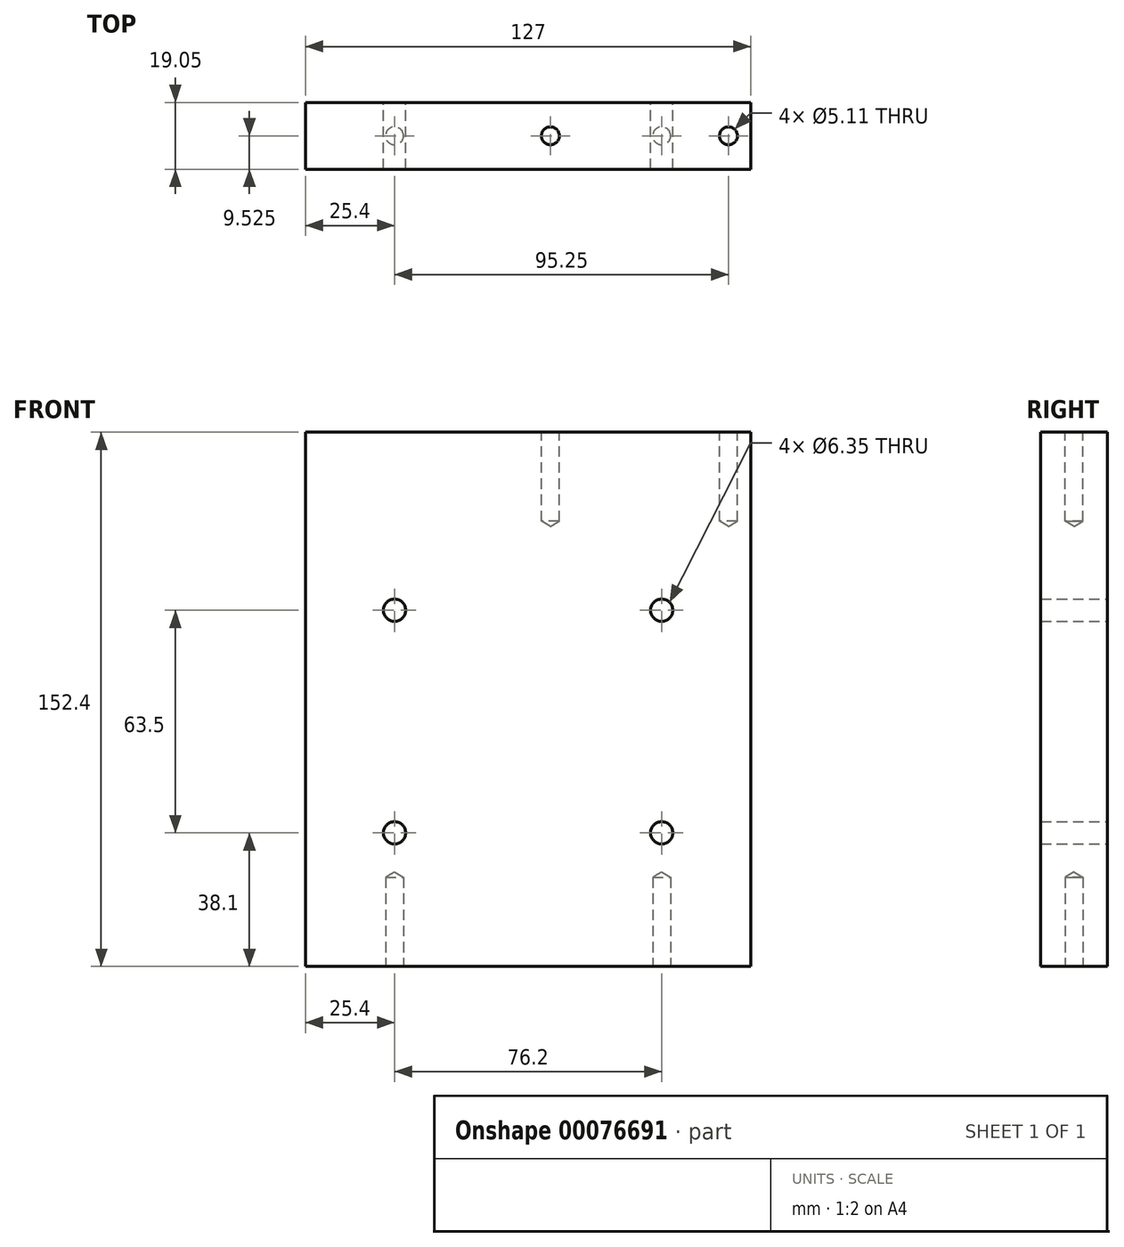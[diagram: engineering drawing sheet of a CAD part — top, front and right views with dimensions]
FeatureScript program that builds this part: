
annotation { "Feature Type Name" : "Feature", "Feature Type Description" : "" }
export const myFeature = defineFeature(function(context is Context, id is Id, definition is map)
    precondition{}
    {
        {
            var Q0;
            Q0=qCreatedBy(makeId("Front.planeOp"),FACE);
            var sketch = newSketch(context, id + "F0", { "sketchPlane" : qUnion([Q0])});
            skLineSegment(sketch, "E0.bottom", {"start": v(0, 0) * mm, "end": v(-127, 0) * mm});
            skLineSegment(sketch, "E0.top", {"start": v(0, 152.4) * mm, "end": v(-127, 152.4) * mm});
            skLineSegment(sketch, "E0.left", {"start": v(0, 0) * mm, "end": v(0, 152.4) * mm});
            skLineSegment(sketch, "E0.right", {"start": v(-127, 0) * mm, "end": v(-127, 152.4) * mm});
            skLineSegment(sketch, "E1.0", {"start": v(-101.6, 0) * mm, "end": v(-101.6, 152.4) * mm, "construction": true});
            skLineSegment(sketch, "E2.0", {"start": v(0, 38.1) * mm, "end": v(-127, 38.1) * mm, "construction": true});
            skLineSegment(sketch, "E3.0", {"start": v(-25.4, 0) * mm, "end": v(-25.4, 152.4) * mm, "construction": true});
            skLineSegment(sketch, "E4.0", {"start": v(0, 101.6) * mm, "end": v(-127, 101.6) * mm, "construction": true});
            skCircle(sketch, "E5", {"center": v(-101.6, 101.6) * mm, "radius": 3.18 * mm});
            skCircle(sketch, "E6", {"center": v(-25.4, 101.6) * mm, "radius": 3.18 * mm});
            skCircle(sketch, "E7", {"center": v(-25.4, 38.1) * mm, "radius": 3.18 * mm});
            skCircle(sketch, "E8", {"center": v(-101.6, 38.1) * mm, "radius": 3.18 * mm});
            skSolve(sketch);
        }
        {
            var Q0;
            Q0=makeQuery(id+"F0.imprint","IMPRINT",FACE,{"disambiguationData":[TD([[makeQuery(id+"F0.imprint","IMPRINT",EDGE,{"derivedFrom":sQuery(id+"F0.wireOp",EDGE,"E0.bottom")}),-1.0]])]});
            extrude(context, id + "F1", {"entities" : qUnion([Q0]), "depth" : 19.05 * mm});
        }
        {
            var Q0;
            Q0=makeQuery(id+"F1.opExtrude","SWEPT_FACE",FACE,{"disambiguationData":[OSD([sQuery(id+"F0.wireOp",EDGE,"E0.bottom")])]});
            var sketch = newSketch(context, id + "F2", { "sketchPlane" : qUnion([Q0])});
            skLineSegment(sketch, "E9.0", {"start": v(-101.6, 19.05) * mm, "end": v(-101.6, 0) * mm, "construction": true});
            skLineSegment(sketch, "E10.0", {"start": v(-25.4, 19.05) * mm, "end": v(-25.4, 0) * mm, "construction": true});
            skLineSegment(sketch, "E11.0", {"start": v(0, 9.53) * mm, "end": v(-127, 9.53) * mm, "construction": true});
            skCircle(sketch, "E12", {"center": v(-101.6, 9.53) * mm, "radius": 2.55 * mm});
            skCircle(sketch, "E13", {"center": v(-25.4, 9.53) * mm, "radius": 2.55 * mm});
            skSolve(sketch);
        }
        {
            var Q0;
            Q0=sQuery(id+"F2.wireOp",VERTEX,"E12.center");
            var Q1;
            Q1=sQuery(id+"F2.wireOp",VERTEX,"E13.center");
            var Q2;
            Q2=makeQuery(id+"F1.opExtrude","SWEPT_BODY",BODY,{"disambiguationData":[OSD([sQuery(id+"F0.wireOp",EDGE,"E0.bottom"),sQuery(id+"F0.wireOp",EDGE,"E0.top"),sQuery(id+"F0.wireOp",EDGE,"E0.left"),sQuery(id+"F0.wireOp",EDGE,"E0.right")])]});
            hole(context, id + "F3", {"style" : HoleStyle.SIMPLE, "endStyle" : HoleEndStyle.BLIND, "holeDiameter" : 5.1 * mm, "holeDepth" : 25.4 * mm, "locations" : qUnion([Q0, Q1]), "scope" : qUnion([Q2])});
        }
        {
            var Q0;
            Q0=makeQuery(id+"F1.opExtrude","SWEPT_FACE",FACE,{"disambiguationData":[OSD([sQuery(id+"F0.wireOp",EDGE,"E0.top")])]});
            var sketch = newSketch(context, id + "F4", { "sketchPlane" : qUnion([Q0])});
            skLineSegment(sketch, "E14.0", {"start": v(-6.35, -19.05) * mm, "end": v(-6.35, 0) * mm, "construction": true});
            skLineSegment(sketch, "E15.0", {"start": v(-57.15, -19.05) * mm, "end": v(-57.15, 0) * mm, "construction": true});
            skCircle(sketch, "E16", {"center": v(-57.15, -9.53) * mm, "radius": 4.34 * mm, "construction": true});
            skCircle(sketch, "E17", {"center": v(-6.35, -9.53) * mm, "radius": 4.86 * mm, "construction": true});
            skSolve(sketch);
        }
        {
            var Q0;
            Q0=sQuery(id+"F4.wireOp",VERTEX,"E16.center");
            var Q1;
            Q1=makeQuery(id+"F1.opExtrude","SWEPT_BODY",BODY,{"disambiguationData":[OSD([sQuery(id+"F0.wireOp",EDGE,"E0.bottom"),sQuery(id+"F0.wireOp",EDGE,"E0.top"),sQuery(id+"F0.wireOp",EDGE,"E0.left"),sQuery(id+"F0.wireOp",EDGE,"E0.right")])]});
            hole(context, id + "F5", {"style" : HoleStyle.SIMPLE, "endStyle" : HoleEndStyle.BLIND, "holeDiameter" : 5.1 * mm, "holeDepth" : 25.4 * mm, "locations" : qUnion([Q0]), "scope" : qUnion([Q1])});
        }
        {
            var Q0;
            Q0=sQuery(id+"F4.wireOp",VERTEX,"E17.center");
            var Q1;
            Q1=makeQuery(id+"F1.opExtrude","SWEPT_BODY",BODY,{"disambiguationData":[OSD([sQuery(id+"F0.wireOp",EDGE,"E0.bottom"),sQuery(id+"F0.wireOp",EDGE,"E0.top"),sQuery(id+"F0.wireOp",EDGE,"E0.left"),sQuery(id+"F0.wireOp",EDGE,"E0.right")])]});
            hole(context, id + "F6", {"style" : HoleStyle.SIMPLE, "endStyle" : HoleEndStyle.BLIND, "holeDiameter" : 5.1 * mm, "holeDepth" : 25.4 * mm, "locations" : qUnion([Q0]), "scope" : qUnion([Q1])});
        }
    });
